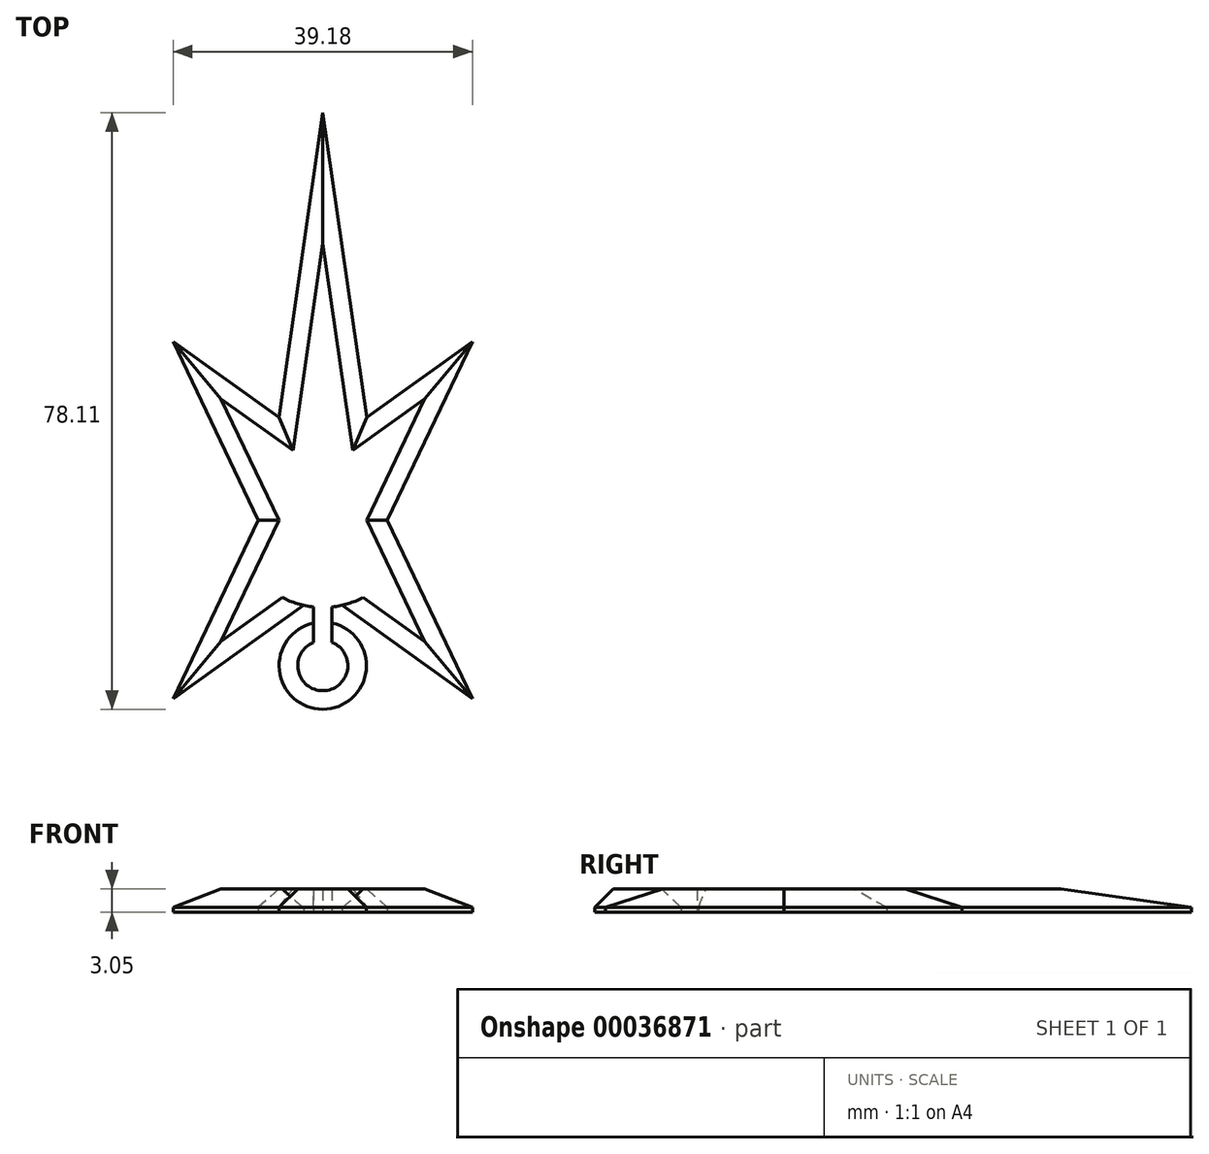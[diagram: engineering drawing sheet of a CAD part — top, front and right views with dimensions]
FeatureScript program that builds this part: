
annotation { "Feature Type Name" : "Feature", "Feature Type Description" : "" }
export const myFeature = defineFeature(function(context is Context, id is Id, definition is map)
    precondition{}
    {
        {
            var Q0;
            Q0=qCreatedBy(makeId("Top.planeOp"),FACE);
            var sketch = newSketch(context, id + "F0", { "sketchPlane" : qUnion([Q0])});
            skArc(sketch, "E0", {"start": v(-8.79, 3.67) * mm, "mid": v(-9.53, 0) * mm, "end": v(-8.79, -3.67) * mm, "construction": true});
            skCircle(sketch, "E1", {"center": v(0, 0) * mm, "radius": 6.35 * mm, "construction": true});
            skLineSegment(sketch, "E2", {"start": v(-59.48, 0) * mm, "end": v(0, 0) * mm, "construction": true});
            skLineSegment(sketch, "E3", {"start": v(0, 0) * mm, "end": v(0, 44.45) * mm, "construction": true});
            skLineSegment(sketch, "E4", {"start": v(0, 44.45) * mm, "end": v(-4.8, 11.23) * mm});
            skLineSegment(sketch, "E5", {"start": v(-4.8, 11.23) * mm, "end": v(-16.33, 19.46) * mm});
            skLineSegment(sketch, "E6", {"start": v(-16.33, 19.46) * mm, "end": v(-7.04, 0) * mm});
            skLineSegment(sketch, "E7.MirrorCS", {"start": v(0, 44.45) * mm, "end": v(4.8, 11.23) * mm});
            skLineSegment(sketch, "E8", {"start": v(0, 0) * mm, "end": v(-16.33, 19.46) * mm, "construction": true});
            skLineSegment(sketch, "E9.MirrorCS", {"start": v(16.33, 19.46) * mm, "end": v(7.04, 0) * mm});
            skLineSegment(sketch, "E10.MirrorCS", {"start": v(4.8, 11.23) * mm, "end": v(16.33, 19.46) * mm});
            skLineSegment(sketch, "E11.MirrorCS", {"start": v(16.33, -19.46) * mm, "end": v(7.04, 0) * mm});
            skLineSegment(sketch, "E12.MirrorCS", {"start": v(2.09, -9.3) * mm, "end": v(16.33, -19.46) * mm});
            skLineSegment(sketch, "E13.MirrorCS", {"start": v(-2.09, -9.3) * mm, "end": v(-16.33, -19.46) * mm});
            skLineSegment(sketch, "E14.MirrorCS", {"start": v(-16.33, -19.46) * mm, "end": v(-7.04, 0) * mm});
            skPoint(sketch, "E15.orphan", {"position": v(-5.27, 7.93) * mm});
            skPoint(sketch, "E16.orphan", {"position": v(-2.09, 9.3) * mm});
            skPoint(sketch, "E17.orphan", {"position": v(2.09, 9.3) * mm});
            skPoint(sketch, "E18.orphan", {"position": v(5.27, 7.93) * mm});
            skArc(sketch, "E19.trimOffspring", {"start": v(-2.09, -9.3) * mm, "mid": v(-1.55, -9.4) * mm, "end": v(-1.02, -9.47) * mm});
            skArc(sketch, "E20.trimOffspring", {"start": v(8.79, -3.67) * mm, "mid": v(9.53, 0) * mm, "end": v(8.79, 3.67) * mm, "construction": true});
            skArc(sketch, "E21", {"start": v(-1.02, -11.22) * mm, "mid": v(0, -20.64) * mm, "end": v(1.02, -11.22) * mm});
            skLineSegment(sketch, "E22.left", {"start": v(-1.02, -9.47) * mm, "end": v(-1.02, -11.22) * mm});
            skLineSegment(sketch, "E22.right", {"start": v(1.02, -9.47) * mm, "end": v(1.02, -11.22) * mm});
            skArc(sketch, "E23.trimOffspring", {"start": v(1.02, -9.47) * mm, "mid": v(1.55, -9.4) * mm, "end": v(2.09, -9.3) * mm});
            skSolve(sketch);
        }
        {
            var Q0;
            Q0 = qSketchRegion(id + "F0", true);
            extrude(context, id + "F1", {"entities" : qUnion([Q0]), "depth" : 2.54 * mm});
        }
        {
            var Q0;
            Q0=makeQuery(id+"F1.opExtrude","CAP_EDGE",EDGE,{"disambiguationData":[OSD([sQuery(id+"F0.wireOp",EDGE,"E4")])],"isStart":false});
            var Q1;
            Q1=makeQuery(id+"F1.opExtrude","CAP_EDGE",EDGE,{"disambiguationData":[OSD([sQuery(id+"F0.wireOp",EDGE,"E10.MirrorCS")])],"isStart":false});
            var Q2;
            Q2=makeQuery(id+"F1.opExtrude","CAP_EDGE",EDGE,{"disambiguationData":[OSD([sQuery(id+"F0.wireOp",EDGE,"E9.MirrorCS")])],"isStart":false});
            var Q3;
            Q3=makeQuery(id+"F1.opExtrude","CAP_EDGE",EDGE,{"disambiguationData":[OSD([sQuery(id+"F0.wireOp",EDGE,"E5")])],"isStart":false});
            var Q4;
            Q4=makeQuery(id+"F1.opExtrude","CAP_EDGE",EDGE,{"disambiguationData":[OSD([sQuery(id+"F0.wireOp",EDGE,"E6")])],"isStart":false});
            var Q5;
            Q5=makeQuery(id+"F1.opExtrude","CAP_EDGE",EDGE,{"disambiguationData":[OSD([sQuery(id+"F0.wireOp",EDGE,"E7.MirrorCS")])],"isStart":false});
            var Q6;
            Q6=makeQuery(id+"F1.opExtrude","CAP_EDGE",EDGE,{"disambiguationData":[OSD([sQuery(id+"F0.wireOp",EDGE,"E11.MirrorCS")])],"isStart":false});
            var Q7;
            Q7=makeQuery(id+"F1.opExtrude","CAP_EDGE",EDGE,{"disambiguationData":[OSD([sQuery(id+"F0.wireOp",EDGE,"E12.MirrorCS")])],"isStart":false});
            var Q8;
            Q8=makeQuery(id+"F1.opExtrude","CAP_EDGE",EDGE,{"disambiguationData":[OSD([sQuery(id+"F0.wireOp",EDGE,"E13.MirrorCS")])],"isStart":false});
            var Q9;
            Q9=makeQuery(id+"F1.opExtrude","CAP_EDGE",EDGE,{"disambiguationData":[OSD([sQuery(id+"F0.wireOp",EDGE,"E14.MirrorCS")])],"isStart":false});
            var Q10;
            Q10=makeQuery(id+"F1.opExtrude","CAP_EDGE",EDGE,{"disambiguationData":[OSD([sQuery(id+"F0.wireOp",EDGE,"E21")])],"isStart":false});
            chamfer(context, id + "F2", {"entities" : qUnion([Q0, Q1, Q2, Q3, Q4, Q5, Q6, Q7, Q8, Q9, Q10]), "width" : 2.03 * mm, "tangentPropagation" : true});
        }
        {
            var Q0;
            Q0=makeQuery(id+"F1.opExtrude","SWEPT_BODY",BODY,{"disambiguationData":[OSD([sQuery(id+"F0.wireOp",EDGE,"E4"),sQuery(id+"F0.wireOp",EDGE,"E5"),sQuery(id+"F0.wireOp",EDGE,"E6"),sQuery(id+"F0.wireOp",EDGE,"E7.MirrorCS"),sQuery(id+"F0.wireOp",EDGE,"E9.MirrorCS"),sQuery(id+"F0.wireOp",EDGE,"E10.MirrorCS"),sQuery(id+"F0.wireOp",EDGE,"E11.MirrorCS"),sQuery(id+"F0.wireOp",EDGE,"E12.MirrorCS"),sQuery(id+"F0.wireOp",EDGE,"E13.MirrorCS"),sQuery(id+"F0.wireOp",EDGE,"E14.MirrorCS"),sQuery(id+"F0.wireOp",EDGE,"E19.trimOffspring"),sQuery(id+"F0.wireOp",EDGE,"E21"),sQuery(id+"F0.wireOp",EDGE,"E22.left"),sQuery(id+"F0.wireOp",EDGE,"E22.right"),sQuery(id+"F0.wireOp",EDGE,"E23.trimOffspring")])]});
            var Q1;
            Q1=qCreatedBy(makeId("Origin.pointOp"),VERTEX);
            transform(context, id + "F3", {"entities" : qUnion([Q0]), "transformType" : TransformType.SCALE_UNIFORMLY, "scale" : 1.2, "makeCopy" : false, "scalePoint" : qUnion([Q1])});
        }
    });
